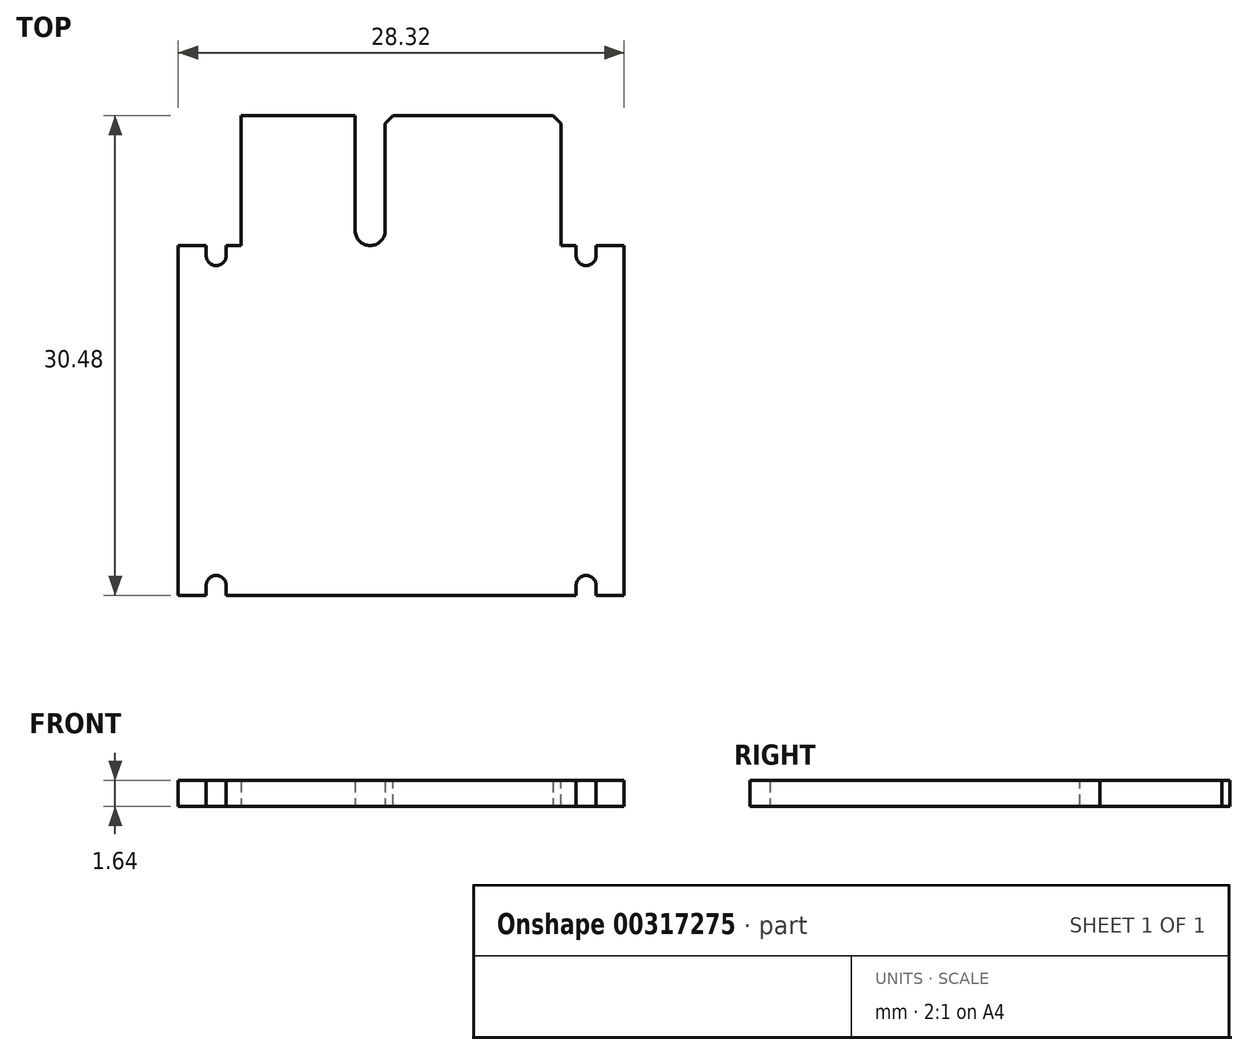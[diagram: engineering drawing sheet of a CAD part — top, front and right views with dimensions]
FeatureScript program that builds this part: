
annotation { "Feature Type Name" : "Feature", "Feature Type Description" : "" }
export const myFeature = defineFeature(function(context is Context, id is Id, definition is map)
    precondition{}
    {
        {
            var Q0;
            Q0=qCreatedBy(makeId("Top.planeOp"),FACE);
            var sketch = newSketch(context, id + "F0", { "sketchPlane" : qUnion([Q0])});
            skLineSegment(sketch, "E0.bottom", {"start": v(14.16, -30.48) * mm, "end": v(-14.16, -30.48) * mm});
            skLineSegment(sketch, "E0.top", {"start": v(14.16, 0) * mm, "end": v(-14.16, 0) * mm});
            skLineSegment(sketch, "E0.left", {"start": v(14.16, -30.48) * mm, "end": v(14.16, 0) * mm});
            skLineSegment(sketch, "E0.right", {"start": v(-14.16, -30.48) * mm, "end": v(-14.16, 0) * mm});
            skPoint(sketch, "E0.middle", {"position": v(0, 0) * mm});
            skSolve(sketch);
        }
        {
            var Q0;
            Q0=qSketchRegion(id+"F0",true);
            extrude(context, id + "F1", {"entities" : qUnion([Q0]), "depth" : 1.64 * mm});
        }
        {
            var Q0;
            Q0=qCreatedBy(makeId("Top.planeOp"),FACE);
            var sketch = newSketch(context, id + "F2", { "sketchPlane" : qUnion([Q0])});
            skLineSegment(sketch, "E1.top", {"start": v(-14.16, 0) * mm, "end": v(-10.16, 0) * mm});
            skLineSegment(sketch, "E1.left", {"start": v(-14.16, -8.25) * mm, "end": v(-14.16, 0) * mm});
            skLineSegment(sketch, "E1.right", {"start": v(-10.16, -8.26) * mm, "end": v(-10.16, 0) * mm});
            skLineSegment(sketch, "E2.bottom", {"start": v(-2.92, -8.26) * mm, "end": v(-1.02, -8.26) * mm});
            skLineSegment(sketch, "E2.top", {"start": v(-2.92, 0) * mm, "end": v(-1.02, 0) * mm});
            skLineSegment(sketch, "E2.left", {"start": v(-2.92, -8.26) * mm, "end": v(-2.92, 0) * mm});
            skLineSegment(sketch, "E2.right", {"start": v(-1.02, -8.26) * mm, "end": v(-1.02, 0) * mm});
            skLineSegment(sketch, "E3.top", {"start": v(14.16, 0) * mm, "end": v(10.16, 0) * mm});
            skLineSegment(sketch, "E3.left", {"start": v(14.16, -8.26) * mm, "end": v(14.16, 0) * mm});
            skLineSegment(sketch, "E3.right", {"start": v(10.16, -8.26) * mm, "end": v(10.16, 0) * mm});
            skLineSegment(sketch, "E4", {"start": v(-14.16, -8.26) * mm, "end": v(-12.38, -8.26) * mm});
            skLineSegment(sketch, "E5", {"start": v(-12.38, -8.26) * mm, "end": v(-12.38, -9.53) * mm});
            skLineSegment(sketch, "E6", {"start": v(-12.38, -9.53) * mm, "end": v(-11.11, -9.53) * mm});
            skLineSegment(sketch, "E7", {"start": v(-11.11, -9.53) * mm, "end": v(-11.11, -8.26) * mm});
            skLineSegment(sketch, "E8", {"start": v(-11.11, -8.26) * mm, "end": v(-10.16, -8.26) * mm});
            skLineSegment(sketch, "E9", {"start": v(10.16, -8.26) * mm, "end": v(11.11, -8.26) * mm});
            skLineSegment(sketch, "E10", {"start": v(11.11, -8.26) * mm, "end": v(11.11, -9.53) * mm});
            skLineSegment(sketch, "E11", {"start": v(11.11, -9.53) * mm, "end": v(12.38, -9.53) * mm});
            skLineSegment(sketch, "E12", {"start": v(12.38, -9.53) * mm, "end": v(12.38, -8.26) * mm});
            skLineSegment(sketch, "E13", {"start": v(12.38, -8.26) * mm, "end": v(14.16, -8.26) * mm});
            skLineSegment(sketch, "E14.bottom", {"start": v(-12.38, -30.48) * mm, "end": v(-11.11, -30.48) * mm});
            skLineSegment(sketch, "E14.top", {"start": v(-12.38, -29.2) * mm, "end": v(-11.11, -29.2) * mm});
            skLineSegment(sketch, "E14.left", {"start": v(-12.38, -30.48) * mm, "end": v(-12.38, -29.2) * mm});
            skLineSegment(sketch, "E14.right", {"start": v(-11.11, -30.48) * mm, "end": v(-11.11, -29.2) * mm});
            skLineSegment(sketch, "E15.bottom", {"start": v(11.11, -30.48) * mm, "end": v(12.38, -30.48) * mm});
            skLineSegment(sketch, "E15.top", {"start": v(11.11, -29.2) * mm, "end": v(12.38, -29.2) * mm});
            skLineSegment(sketch, "E15.left", {"start": v(11.11, -30.48) * mm, "end": v(11.11, -29.21) * mm});
            skLineSegment(sketch, "E15.right", {"start": v(12.38, -30.48) * mm, "end": v(12.38, -29.21) * mm});
            skLineSegment(sketch, "E16", {"start": v(-20.57, -19.37) * mm, "end": v(25.43, -19.37) * mm, "construction": true});
            skPoint(sketch, "E17", {"position": v(-11.75, -9.53) * mm});
            skPoint(sketch, "E18", {"position": v(11.75, -9.53) * mm});
            skSolve(sketch);
        }
        {
            var Q0;
            Q0=qSketchRegion(id+"F2",true);
            extrude(context, id + "F3", {"entities" : qUnion([Q0]), "operationType" : NewBodyOperationType.REMOVE, "depth" : 25 * mm});
        }
        {
            var Q0;
            Q0=makeQuery(id+"F3.boolean.opBoolean","COPY",EDGE,{"derivedFrom":makeQuery(id+"F3.opExtrude","SWEPT_EDGE",EDGE,{"disambiguationData":[OSD([sQuery(id+"F2.wireOp",EDGE,"E2.bottom"),sQuery(id+"F2.wireOp",EDGE,"E2.left")])]})});
            var Q1;
            Q1=makeQuery(id+"F3.boolean.opBoolean","COPY",EDGE,{"derivedFrom":makeQuery(id+"F3.opExtrude","SWEPT_EDGE",EDGE,{"disambiguationData":[OSD([sQuery(id+"F2.wireOp",EDGE,"E2.bottom"),sQuery(id+"F2.wireOp",EDGE,"E2.right")])]})});
            fillet(context, id + "F4", {"entities" : qUnion([Q0, Q1]), "radius" : (1.9 / 2) * mm, "tangentPropagation" : true, "allowEdgeOverflow" : false});
        }
        {
            var Q0;
            Q0=makeQuery(id+"F3.boolean.opBoolean","COPY",EDGE,{"derivedFrom":makeQuery(id+"F3.opExtrude","SWEPT_EDGE",EDGE,{"disambiguationData":[OSD([sQuery(id+"F2.wireOp",EDGE,"E3.top"),sQuery(id+"F2.wireOp",EDGE,"E3.right")])]})});
            var Q1;
            Q1=makeQuery(id+"F3.boolean.opBoolean","COPY",EDGE,{"derivedFrom":makeQuery(id+"F3.opExtrude","SWEPT_EDGE",EDGE,{"disambiguationData":[OSD([sQuery(id+"F2.wireOp",EDGE,"E2.top"),sQuery(id+"F2.wireOp",EDGE,"E2.right")])]})});
            var Q2;
            Q2=makeQuery(id+"F3.boolean.opBoolean","COPY",EDGE,{"derivedFrom":makeQuery(id+"F3.opExtrude","SWEPT_EDGE",EDGE,{"disambiguationData":[OSD([sQuery(id+"F2.wireOp",EDGE,"E2.top"),sQuery(id+"F2.wireOp",EDGE,"E2.left")])]})});
            var Q3;
            Q3=makeQuery(id+"F3.boolean.opBoolean","COPY",EDGE,{"derivedFrom":makeQuery(id+"F3.opExtrude","SWEPT_EDGE",EDGE,{"disambiguationData":[OSD([sQuery(id+"F2.wireOp",EDGE,"E1.top"),sQuery(id+"F2.wireOp",EDGE,"E1.right")])]})});
            chamfer(context, id + "F5", {"entities" : qUnion([Q0, Q1, Q2, Q3]), "width" : 0.5 * mm, "tangentPropagation" : true});
        }
        {
            var Q0;
            Q0=makeQuery(id+"F3.boolean.opBoolean","COPY",EDGE,{"derivedFrom":makeQuery(id+"F3.opExtrude","SWEPT_EDGE",EDGE,{"disambiguationData":[OSD([sQuery(id+"F2.wireOp",EDGE,"E15.top"),sQuery(id+"F2.wireOp",EDGE,"E15.right")])]})});
            var Q1;
            Q1=makeQuery(id+"F3.boolean.opBoolean","COPY",EDGE,{"derivedFrom":makeQuery(id+"F3.opExtrude","SWEPT_EDGE",EDGE,{"disambiguationData":[OSD([sQuery(id+"F2.wireOp",EDGE,"E14.top"),sQuery(id+"F2.wireOp",EDGE,"E14.left")])]})});
            var Q2;
            Q2=makeQuery(id+"F3.boolean.opBoolean","COPY",EDGE,{"derivedFrom":makeQuery(id+"F3.opExtrude","SWEPT_EDGE",EDGE,{"disambiguationData":[OSD([sQuery(id+"F2.wireOp",EDGE,"E14.top"),sQuery(id+"F2.wireOp",EDGE,"E14.right")])]})});
            var Q3;
            Q3=makeQuery(id+"F3.boolean.opBoolean","COPY",EDGE,{"derivedFrom":makeQuery(id+"F3.opExtrude","SWEPT_EDGE",EDGE,{"disambiguationData":[OSD([sQuery(id+"F2.wireOp",EDGE,"E15.top"),sQuery(id+"F2.wireOp",EDGE,"E15.left")])]})});
            var Q4;
            Q4=makeQuery(id+"F3.boolean.opBoolean","COPY",EDGE,{"derivedFrom":makeQuery(id+"F3.opExtrude","SWEPT_EDGE",EDGE,{"disambiguationData":[OSD([sQuery(id+"F2.wireOp",EDGE,"E10"),sQuery(id+"F2.wireOp",EDGE,"E11")])]})});
            var Q5;
            Q5=makeQuery(id+"F3.boolean.opBoolean","COPY",EDGE,{"derivedFrom":makeQuery(id+"F3.opExtrude","SWEPT_EDGE",EDGE,{"disambiguationData":[OSD([sQuery(id+"F2.wireOp",EDGE,"E11"),sQuery(id+"F2.wireOp",EDGE,"E12")])]})});
            var Q6;
            Q6=makeQuery(id+"F3.boolean.opBoolean","COPY",EDGE,{"derivedFrom":makeQuery(id+"F3.opExtrude","SWEPT_EDGE",EDGE,{"disambiguationData":[OSD([sQuery(id+"F2.wireOp",EDGE,"E5"),sQuery(id+"F2.wireOp",EDGE,"E6")])]})});
            var Q7;
            Q7=makeQuery(id+"F3.boolean.opBoolean","COPY",EDGE,{"derivedFrom":makeQuery(id+"F3.opExtrude","SWEPT_EDGE",EDGE,{"disambiguationData":[OSD([sQuery(id+"F2.wireOp",EDGE,"E6"),sQuery(id+"F2.wireOp",EDGE,"E7")])]})});
            fillet(context, id + "F6", {"entities" : qUnion([Q0, Q1, Q2, Q3, Q4, Q5, Q6, Q7]), "radius" : 1.27 * mm / 2, "tangentPropagation" : true, "allowEdgeOverflow" : false});
        }
    });
